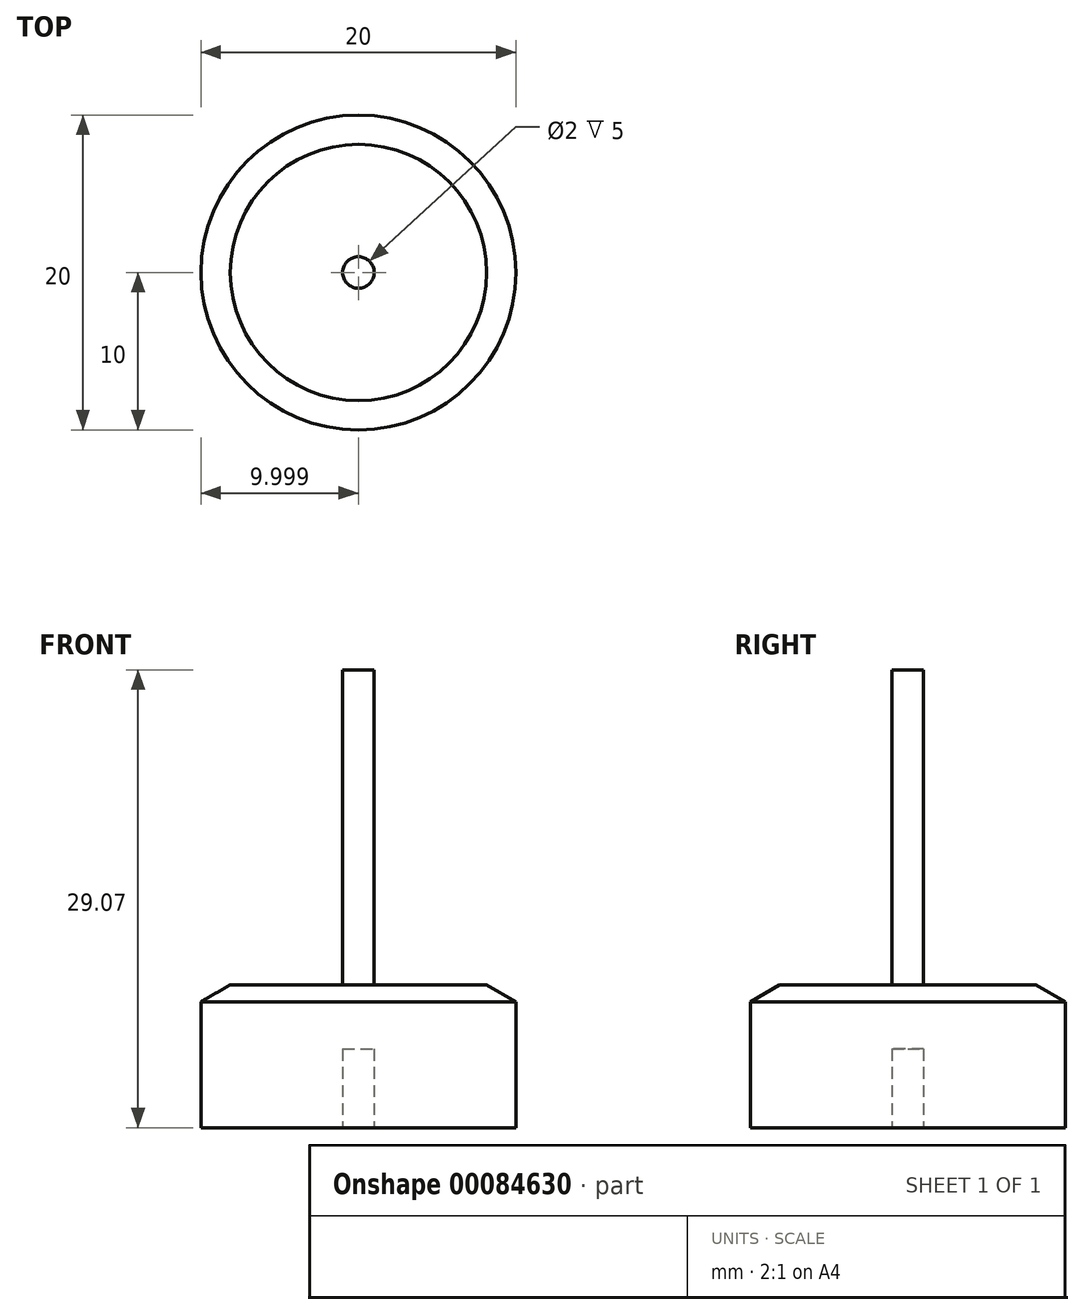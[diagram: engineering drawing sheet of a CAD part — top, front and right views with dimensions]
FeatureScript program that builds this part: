
annotation { "Feature Type Name" : "Feature", "Feature Type Description" : "" }
export const myFeature = defineFeature(function(context is Context, id is Id, definition is map)
    precondition{}
    {
        {
            var Q0;
            Q0=qCreatedBy(makeId("Front.planeOp"),FACE);
            var sketch = newSketch(context, id + "F0", { "sketchPlane" : qUnion([Q0])});
            skLineSegment(sketch, "E0.bottom", {"start": v(-30.55, 8) * mm, "end": v(-20.55, 8) * mm});
            skLineSegment(sketch, "E0.top", {"start": v(-30.55, 0) * mm, "end": v(-21.55, 0) * mm});
            skLineSegment(sketch, "E0.left", {"start": v(-30.55, 8) * mm, "end": v(-30.55, 0) * mm});
            skPoint(sketch, "E1", {"position": v(-20.55, 8) * mm});
            skPoint(sketch, "E2", {"position": v(-20.55, 0) * mm});
            skPoint(sketch, "E3", {"position": v(-20.55, 9.07) * mm});
            skLineSegment(sketch, "E4", {"start": v(-20.55, 8) * mm, "end": v(-20.55, 9.07) * mm});
            skLineSegment(sketch, "E5", {"start": v(-30.55, 8) * mm, "end": v(-28.7, 9.07) * mm});
            skLineSegment(sketch, "E6", {"start": v(-28.7, 9.07) * mm, "end": v(-20.55, 9.07) * mm});
            skLineSegment(sketch, "E7", {"start": v(-20.55, 8) * mm, "end": v(-20.55, 5) * mm});
            skPoint(sketch, "E0.right.end.orphan", {"position": v(-10.55, 0) * mm});
            skPoint(sketch, "E8.start.orphan", {"position": v(-10.55, 8) * mm});
            skLineSegment(sketch, "E9", {"start": v(-20.55, 9.07) * mm, "end": v(-20.55, 29.07) * mm});
            skLineSegment(sketch, "E10", {"start": v(-20.55, 29.07) * mm, "end": v(-21.55, 29.07) * mm});
            skLineSegment(sketch, "E11", {"start": v(-21.55, 29.07) * mm, "end": v(-21.55, 0) * mm});
            skPoint(sketch, "E12.start.orphan", {"position": v(-20.55, 4) * mm});
            skLineSegment(sketch, "E13", {"start": v(-20.55, 5) * mm, "end": v(-21.55, 5) * mm});
            skPoint(sketch, "E14", {"position": v(-20.55, 5) * mm});
            skSolve(sketch);
        }
        {
            var Q0;
            {var subQ0=sQuery(id+"F0.wireOp",EDGE,"E9");Q0=makeQuery(id+"F0.imprint","IMPRINT",FACE,{"disambiguationData":[TD([[makeQuery(id+"F0.imprint","IMPRINT",EDGE,{"derivedFrom":subQ0}),1.0]])]});}
            var Q1;
            {var subQ5=sQuery(id+"F0.wireOp",EDGE,"E0.top");Q1=makeQuery(id+"F0.imprint","IMPRINT",FACE,{"disambiguationData":[TD([[makeQuery(id+"F0.imprint","IMPRINT",EDGE,{"derivedFrom":subQ5}),1.0]])]});}
            var Q2;
            {var subQ0=sQuery(id+"F0.wireOp",EDGE,"E5");Q2=makeQuery(id+"F0.imprint","IMPRINT",FACE,{"disambiguationData":[TD([[makeQuery(id+"F0.imprint","IMPRINT",EDGE,{"derivedFrom":subQ0}),-1.0]])]});}
            var Q3;
            {var subQ0=sQuery(id+"F0.wireOp",EDGE,"E7");Q3=makeQuery(id+"F0.imprint","IMPRINT",FACE,{"disambiguationData":[TD([[makeQuery(id+"F0.imprint","IMPRINT",EDGE,{"derivedFrom":subQ0}),-1.0]])]});}
            var Q4;
            {var subQ0=sQuery(id+"F0.wireOp",EDGE,"E4");Q4=makeQuery(id+"F0.imprint","IMPRINT",FACE,{"disambiguationData":[TD([[makeQuery(id+"F0.imprint","IMPRINT",EDGE,{"derivedFrom":subQ0}),1.0]])]});}
            var Q5;
            Q5=sQuery(id+"F0.wireOp",EDGE,"E9");
            revolve(context, id + "F1", {"entities" : qUnion([Q0, Q1, Q2, Q3, Q4]), "axis" : qUnion([Q5]), "revolveType" : RevolveType.FULL});
        }
    });
